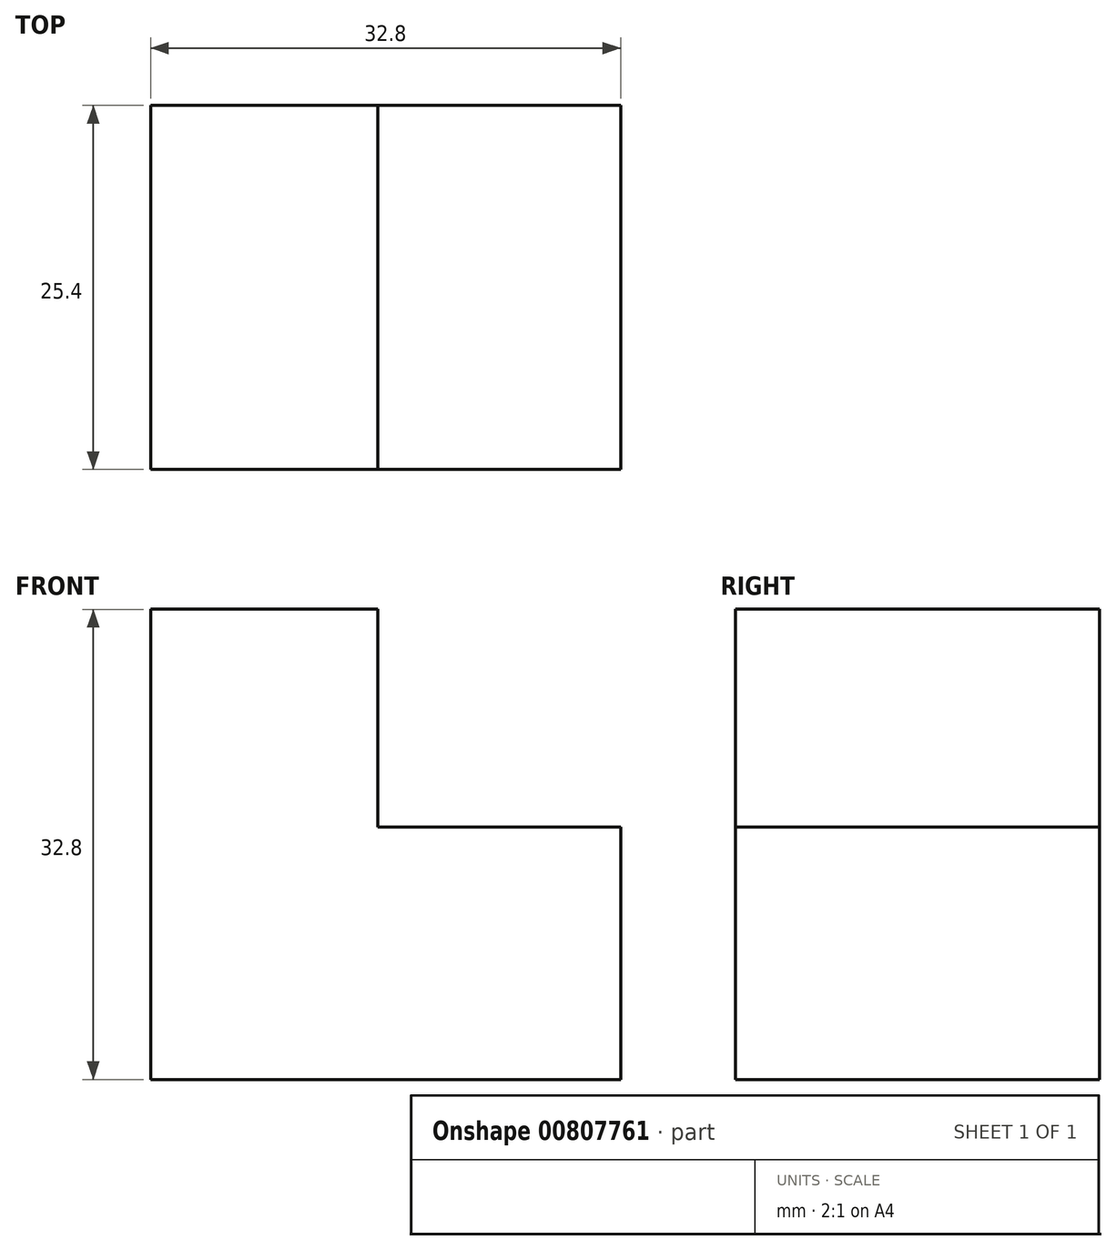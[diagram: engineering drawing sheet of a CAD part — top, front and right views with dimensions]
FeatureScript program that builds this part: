
annotation { "Feature Type Name" : "Feature", "Feature Type Description" : "" }
export const myFeature = defineFeature(function(context is Context, id is Id, definition is map)
    precondition{}
    {
        {
            var Q0;
            Q0=qCreatedBy(makeId("Front.planeOp"),FACE);
            var sketch = newSketch(context, id + "F0", { "sketchPlane" : qUnion([Q0])});
            skLineSegment(sketch, "E0", {"start": v(0, 0) * mm, "end": v(0, 32.8) * mm});
            skLineSegment(sketch, "E1", {"start": v(0, 32.8) * mm, "end": v(15.87, 32.8) * mm});
            skLineSegment(sketch, "E2", {"start": v(15.87, 32.8) * mm, "end": v(15.87, 17.62) * mm});
            skLineSegment(sketch, "E3", {"start": v(17.62, 17.62) * mm, "end": v(32.8, 17.62) * mm});
            skLineSegment(sketch, "E4", {"start": v(15.87, 17.62) * mm, "end": v(19.56, 17.62) * mm});
            skLineSegment(sketch, "E5", {"start": v(32.8, 17.62) * mm, "end": v(32.8, 0) * mm});
            skLineSegment(sketch, "E6", {"start": v(0, 0) * mm, "end": v(32.8, 0) * mm});
            skSolve(sketch);
        }
        {
            var Q0;
            Q0=makeQuery(id+"F0.imprint","IMPRINT",FACE,{"disambiguationData":[TD([[makeQuery(id+"F0.imprint","IMPRINT",EDGE,{"derivedFrom":sQuery(id+"F0.wireOp",EDGE,"E0")}),-1.0]])]});
            extrude(context, id + "F1", {"entities" : qUnion([Q0]), "depth" : 25.4 * mm, "offsetDistance" : 25.4 * mm});
        }
    });
